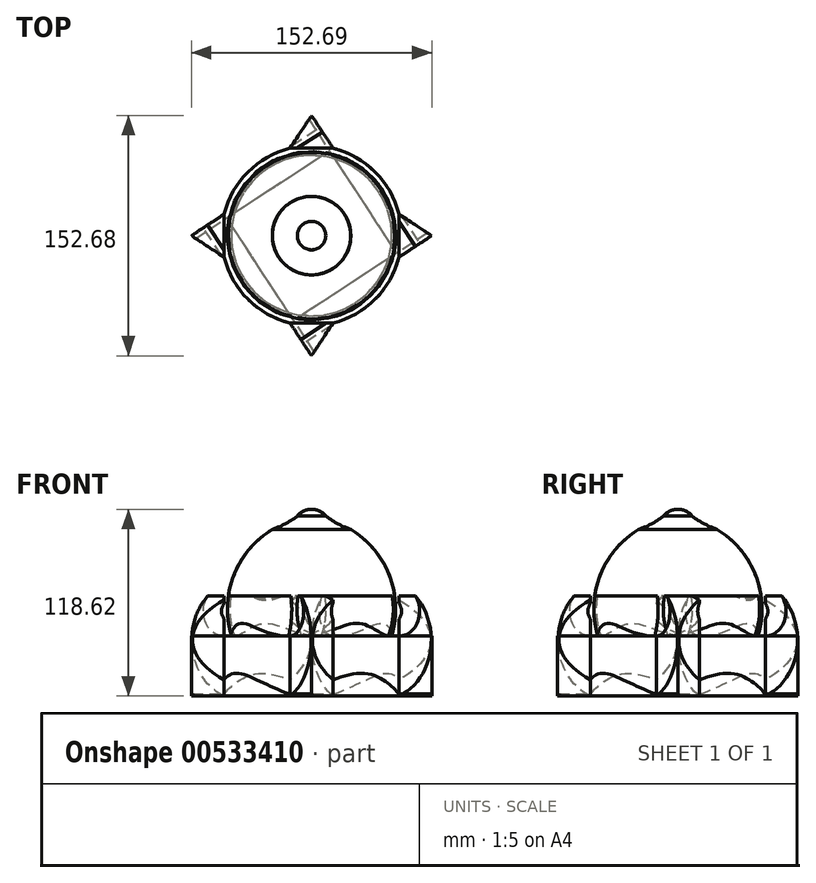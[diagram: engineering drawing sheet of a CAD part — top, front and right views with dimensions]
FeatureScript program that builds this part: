
annotation { "Feature Type Name" : "Feature", "Feature Type Description" : "" }
export const myFeature = defineFeature(function(context is Context, id is Id, definition is map)
    precondition{}
    {
        {
            var Q0;
            Q0=qCreatedBy(makeId("Front.planeOp"),FACE);
            var sketch = newSketch(context, id + "F0", { "sketchPlane" : qUnion([Q0])});
            skLineSegment(sketch, "E0", {"start": v(-33.22, -14.12) * mm, "end": v(17.73, -14.12) * mm});
            skLineSegment(sketch, "E1", {"start": v(17.73, -14.12) * mm, "end": v(17.73, 62.1) * mm});
            skArc(sketch, "E2", {"start": v(-7.2, 53.7) * mm, "mid": v(-31.76, 24.22) * mm, "end": v(-33.22, -14.12) * mm});
            skPoint(sketch, "E3.center.orphan", {"position": v(17.73, 23.99) * mm});
            skEllipticalArc(sketch, "E4", {});
            skArc(sketch, "E5", {"start": v(-7.2, 53.7) * mm, "mid": v(1.12, 57.2) * mm, "end": v(8.68, 62.12) * mm});
            skLineSegment(sketch, "E6", {"start": v(17.73, 62.1) * mm, "end": v(17.73, 66.4) * mm});
            skPoint(sketch, "E7.orphan", {"position": v(68.67, -14.12) * mm});
            skLineSegment(sketch, "E8", {"start": v(8.68, 62.12) * mm, "end": v(8.69, 62.13) * mm});
            const initialGuessF0  = {"E4": [0.01772595630884171, 0.05654634162783623, 0, 1, 0.009850948470117023, 0.010973460585103359, 6.283185307179586, 0.9680867333950314]};
            skSetInitialGuess(sketch, initialGuessF0);
            skSolve(sketch);
        }
        {
            var Q0;
            Q0=makeQuery(id+"F0.imprint","IMPRINT",FACE,{"disambiguationData":[TD([[makeQuery(id+"F0.imprint","IMPRINT",EDGE,{"derivedFrom":sQuery(id+"F0.wireOp",EDGE,"E0")}),1.0]])]});
            var Q1;
            Q1=sQuery(id+"F0.wireOp",EDGE,"E6");
            revolve(context, id + "F1", {"entities" : qUnion([Q0]), "axis" : qUnion([Q1]), "revolveType" : RevolveType.FULL});
        }
        {
            var Q0;
            Q0=makeQuery(id+"F1.opRevolve","SWEPT_FACE",FACE,{"disambiguationData":[OSD([sQuery(id+"F0.wireOp",EDGE,"E0")])]});
            var sketch = newSketch(context, id + "F2", { "sketchPlane" : qUnion([Q0])});
            skCircle(sketch, "E9", {"center": v(17.73, 0) * mm, "radius": 57.15 * mm});
            skLineSegment(sketch, "E10", {"start": v(-58.62, 0) * mm, "end": v(-29.52, 19.05) * mm});
            skLineSegment(sketch, "E11", {"start": v(-58.62, 0) * mm, "end": v(-29.52, -19.05) * mm});
            skLineSegment(sketch, "E12", {"start": v(17.73, -76.34) * mm, "end": v(-1.32, -47.25) * mm});
            skLineSegment(sketch, "E13", {"start": v(17.73, -76.34) * mm, "end": v(36.78, -47.25) * mm});
            skLineSegment(sketch, "E14", {"start": v(17.73, 76.34) * mm, "end": v(36.78, 47.25) * mm});
            skLineSegment(sketch, "E15", {"start": v(-1.32, 47.25) * mm, "end": v(17.73, 76.34) * mm});
            skLineSegment(sketch, "E16", {"start": v(94.07, 0) * mm, "end": v(64.97, 19.05) * mm});
            skLineSegment(sketch, "E17", {"start": v(94.07, 0) * mm, "end": v(64.97, -19.05) * mm});
            skArc(sketch, "E18", {"start": v(-29.52, -19.05) * mm, "mid": v(-18.3, -36.02) * mm, "end": v(-1.32, -47.25) * mm});
            skArc(sketch, "E19.trimOffspring", {"start": v(-1.32, 47.25) * mm, "mid": v(-18.3, 36.02) * mm, "end": v(-29.52, 19.05) * mm});
            skArc(sketch, "E20.trimOffspring", {"start": v(64.97, 19.05) * mm, "mid": v(53.75, 36.02) * mm, "end": v(36.78, 47.25) * mm});
            skArc(sketch, "E21.trimOffspring", {"start": v(36.78, -47.25) * mm, "mid": v(53.75, -36.02) * mm, "end": v(64.97, -19.05) * mm});
            skSolve(sketch);
        }
        {
            var Q0;
            Q0 = qSketchRegion(id + "F2", true);
            extrude(context, id + "F3", {"entities" : qUnion([Q0]), "operationType" : NewBodyOperationType.ADD, "depth" : 38.1 * mm, "offsetDistance" : 25.4 * mm});
        }
        {
            var Q0;
            Q0=makeQuery(id+"F3.opExtrude","CAP_FACE",FACE,{"disambiguationData":[OSD([sQuery(id+"F2.wireOp",EDGE,"E9"),sQuery(id+"F2.wireOp",EDGE,"E10"),sQuery(id+"F2.wireOp",EDGE,"E11"),sQuery(id+"F2.wireOp",EDGE,"E12"),sQuery(id+"F2.wireOp",EDGE,"E13"),sQuery(id+"F2.wireOp",EDGE,"E14"),sQuery(id+"F2.wireOp",EDGE,"E15"),sQuery(id+"F2.wireOp",EDGE,"E16"),sQuery(id+"F2.wireOp",EDGE,"E17")])],"isStart":true});
            var sketch = newSketch(context, id + "F4", { "sketchPlane" : qUnion([Q0])});
            skLineSegment(sketch, "E22", {"start": v(17.73, 76.34) * mm, "end": v(4.08, 55.5) * mm});
            skLineSegment(sketch, "E23", {"start": v(4.08, 55.5) * mm, "end": v(31.37, 55.5) * mm});
            skLineSegment(sketch, "E24", {"start": v(31.37, 55.5) * mm, "end": v(17.73, 76.34) * mm});
            skSolve(sketch);
        }
        {
            var Q0;
            Q0=makeQuery(id+"F4.imprint","IMPRINT",FACE,{"disambiguationData":[TD([[makeQuery(id+"F4.imprint","IMPRINT",EDGE,{"derivedFrom":sQuery(id+"F4.wireOp",EDGE,"E22")}),1.0]])]});
            extrude(context, id + "F5", {"entities" : qUnion([Q0]), "operationType" : NewBodyOperationType.ADD, "depth" : 25.4 * mm, "offsetDistance" : 25.4 * mm});
        }
        {
            var Q0;
            Q0=makeQuery(id+"F5.boolean.opBoolean","MERGE",FACE,{"derivedFrom":[makeQuery(id+"F3.opExtrude","SWEPT_FACE",FACE,{"disambiguationData":[OSD([sQuery(id+"F2.wireOp",EDGE,"E13")])]}),makeQuery(id+"F5.opExtrude","SWEPT_FACE",FACE,{"disambiguationData":[OSD([sQuery(id+"F4.wireOp",EDGE,"E24")])]})]});
            var sketch = newSketch(context, id + "F6", { "sketchPlane" : qUnion([Q0])});
            skLineSegment(sketch, "E25", {"start": v(54.16, -14.12) * mm, "end": v(54.16, 11.28) * mm});
            skArc(sketch, "E26", {"start": v(29.24, -14.12) * mm, "mid": v(43.39, -5.3) * mm, "end": v(41.7, 11.28) * mm});
            skArc(sketch, "E27", {"start": v(29.24, -52.22) * mm, "mid": v(53.11, -23.93) * mm, "end": v(41.7, 11.28) * mm});
            skSolve(sketch);
        }
        {
            var Q0;
            {var subQ0=sQuery(id+"F6.wireOp",EDGE,"E26");Q0=makeQuery(id+"F6.imprint","IMPRINT",FACE,{"disambiguationData":[TD([[makeQuery(id+"F6.imprint","IMPRINT",EDGE,{"derivedFrom":subQ0}),1.0]])]});}
            var Q1;
            {var subQ4=sQuery(id+"F6.wireOp",EDGE,"E25");Q1=makeQuery(id+"F6.imprint","IMPRINT",FACE,{"disambiguationData":[TD([[makeQuery(id+"F6.imprint","IMPRINT",EDGE,{"derivedFrom":subQ4}),1.0]])]});}
            extrude(context, id + "F7", {"entities" : qUnion([Q0, Q1]), "operationType" : NewBodyOperationType.REMOVE, "endBound" : BoundingType.THROUGH_ALL, "oppositeDirection" : true, "depth" : 25.4 * mm, "offsetDistance" : 25.4 * mm});
        }
        {
            var Q0;
            Q0=makeQuery(id+"F7.boolean.opBoolean","SPLIT",BODY,{"disambiguationData":[OD(1.0)],"derivedFrom":makeQuery(id+"F1.opRevolve","SWEPT_BODY",BODY,{"disambiguationData":[OSD([sQuery(id+"F0.wireOp",EDGE,"E0"),sQuery(id+"F0.wireOp",EDGE,"E1"),sQuery(id+"F0.wireOp",EDGE,"E2"),sQuery(id+"F0.wireOp",EDGE,"E4"),sQuery(id+"F0.wireOp",EDGE,"E5"),sQuery(id+"F0.wireOp",EDGE,"E6"),sQuery(id+"F0.wireOp",EDGE,"E8")])]})});
            var Q1;
            Q1=makeQuery(id+"F1.opRevolve","SWEPT_FACE",FACE,{"disambiguationData":[OSD([sQuery(id+"F0.wireOp",EDGE,"E4")])]});
            circularPattern(context, id + "F8", {"entities" : qUnion([Q0]), "axis" : qUnion([Q1]), "angle" : 360 * degree, "instanceCount" : 4, "equalSpace" : true});
        }
    });
